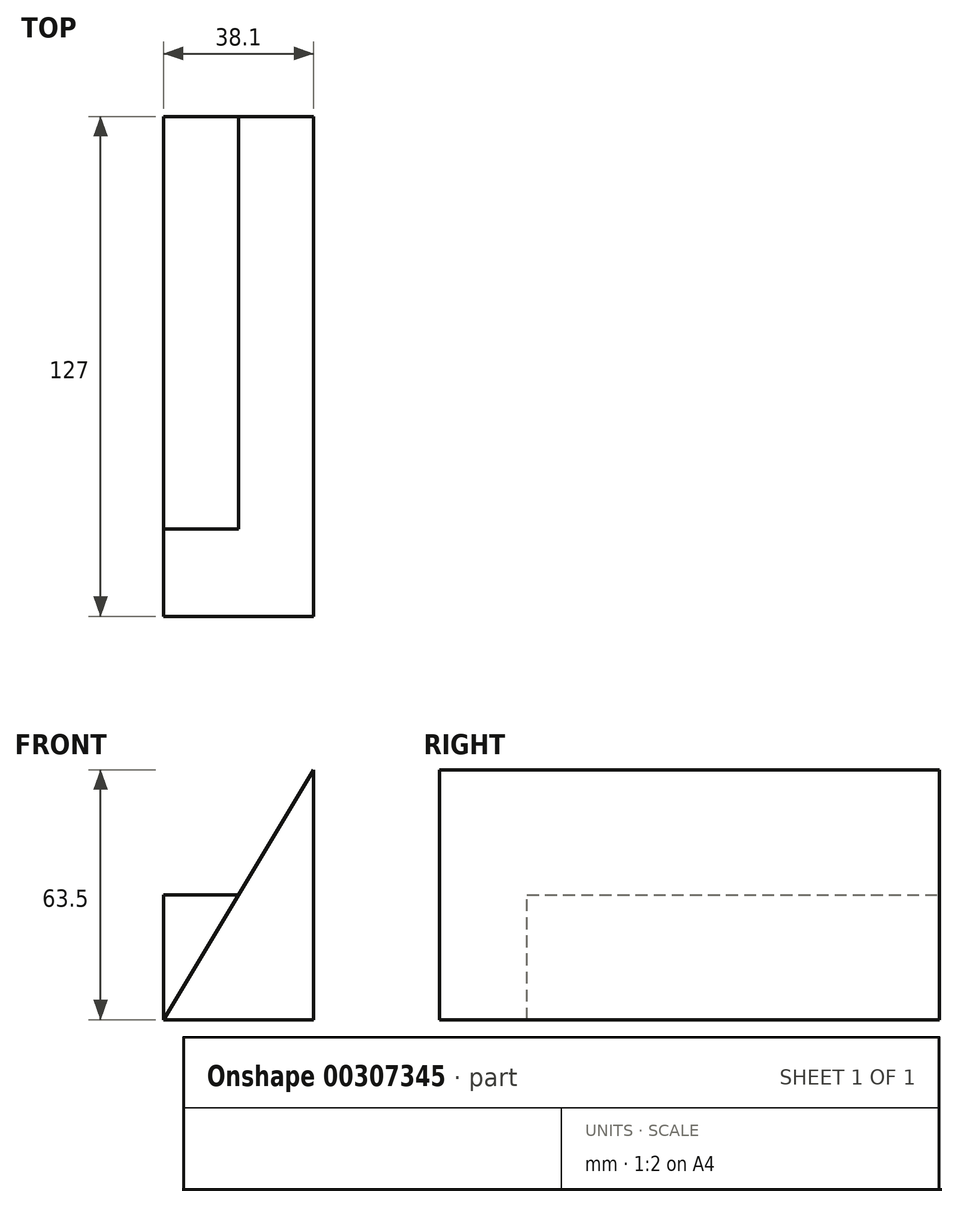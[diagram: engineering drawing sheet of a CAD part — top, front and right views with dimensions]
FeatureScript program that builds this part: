
annotation { "Feature Type Name" : "Feature", "Feature Type Description" : "" }
export const myFeature = defineFeature(function(context is Context, id is Id, definition is map)
    precondition{}
    {
        {
            var Q0;
            Q0=qCreatedBy(makeId("Front.planeOp"),FACE);
            var sketch = newSketch(context, id + "F0", { "sketchPlane" : qUnion([Q0])});
            skLineSegment(sketch, "E0", {"start": v(-23, 31.75) * mm, "end": v(-23, -31.75) * mm});
            skLineSegment(sketch, "E1", {"start": v(-23, -31.75) * mm, "end": v(-61.1, -31.75) * mm});
            skLineSegment(sketch, "E2", {"start": v(-61.1, -31.75) * mm, "end": v(-23, 31.75) * mm});
            skPoint(sketch, "E3.start.orphan", {"position": v(-42.05, 0) * mm});
            skLineSegment(sketch, "E4", {"start": v(-61.1, -31.75) * mm, "end": v(-61.1, 0) * mm});
            skLineSegment(sketch, "E5", {"start": v(-61.1, 0) * mm, "end": v(-42.05, 0) * mm});
            skSolve(sketch);
        }
        {
            var Q0;
            {var subQ0=sQuery(id+"F0.wireOp",EDGE,"E0");Q0=makeQuery(id+"F0.imprint","IMPRINT",FACE,{"disambiguationData":[TD([[makeQuery(id+"F0.imprint","IMPRINT",EDGE,{"derivedFrom":subQ0}),-1.0]])]});}
            extrude(context, id + "F1", {"entities" : qUnion([Q0]), "depth" : 127 * mm});
        }
        {
            var Q0;
            {var subQ0=sQuery(id+"F0.wireOp",EDGE,"E4");Q0=makeQuery(id+"F0.imprint","IMPRINT",FACE,{"disambiguationData":[TD([[makeQuery(id+"F0.imprint","IMPRINT",EDGE,{"derivedFrom":subQ0}),-1.0]])]});}
            extrude(context, id + "F2", {"entities" : qUnion([Q0]), "operationType" : NewBodyOperationType.ADD, "depth" : 104.77 * mm, "hasSecondDirection" : true, "secondDirectionOppositeDirection" : false, "secondDirectionDepth" : 7 / 203.2 * mm});
        }
    });
